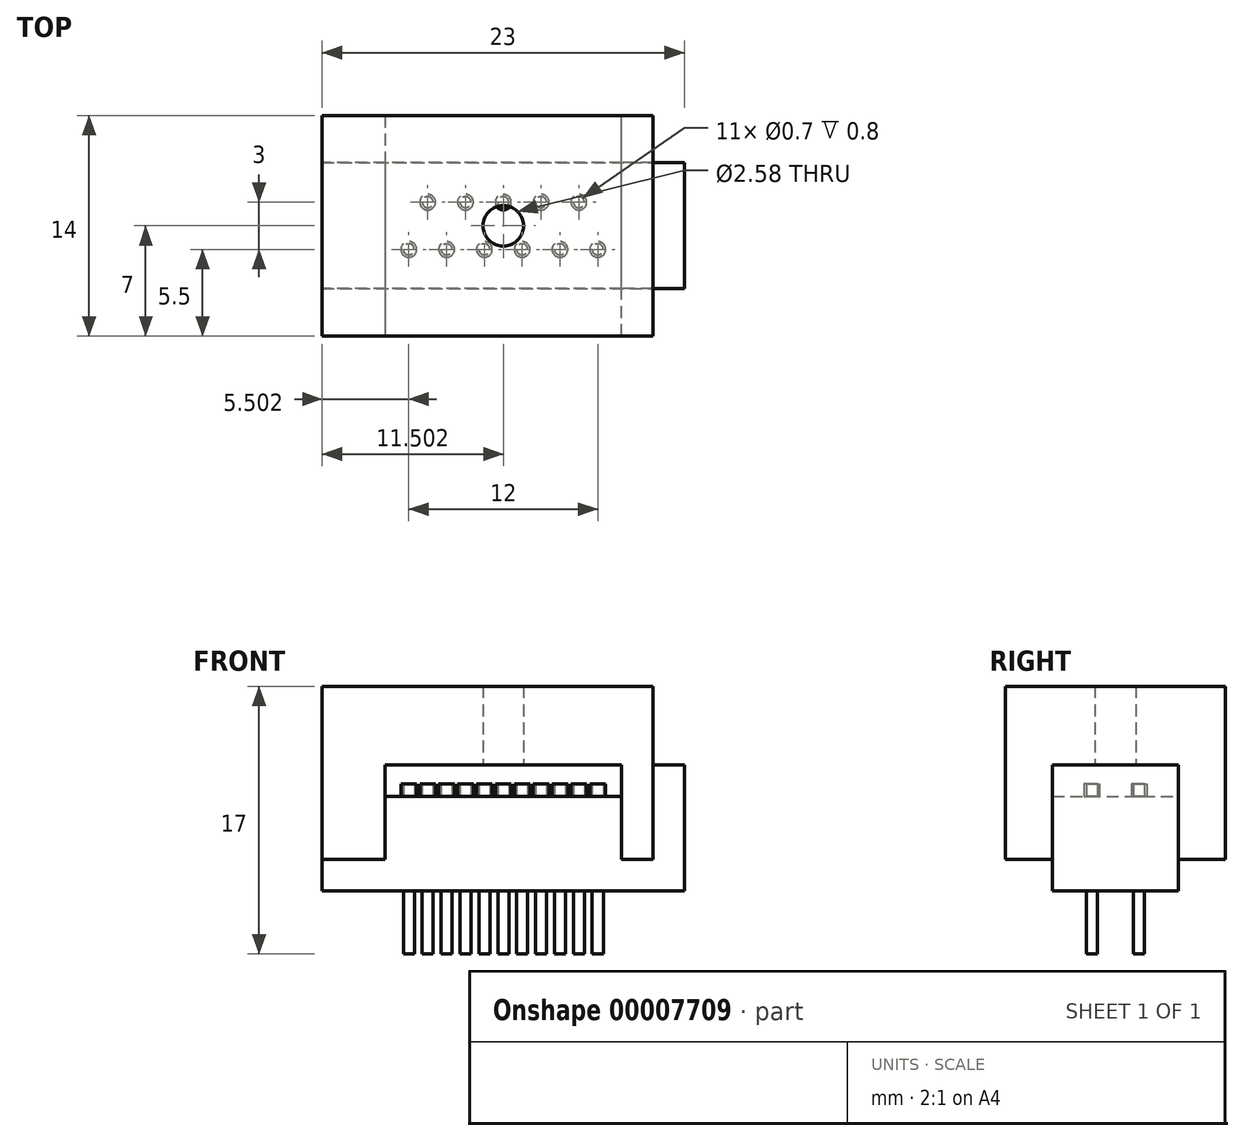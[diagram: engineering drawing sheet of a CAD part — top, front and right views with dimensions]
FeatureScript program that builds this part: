
annotation { "Feature Type Name" : "Feature", "Feature Type Description" : "" }
export const myFeature = defineFeature(function(context is Context, id is Id, definition is map)
    precondition{}
    {
        {
            var Q0;
            Q0=qCreatedBy(makeId("Front.planeOp"),FACE);
            var sketch = newSketch(context, id + "F0", { "sketchPlane" : qUnion([Q0])});
            skLineSegment(sketch, "E0", {"start": v(-36.77, -24.61) * mm, "end": v(-13.77, -24.61) * mm});
            skLineSegment(sketch, "E1", {"start": v(-13.77, -24.61) * mm, "end": v(-13.77, -16.61) * mm});
            skLineSegment(sketch, "E2", {"start": v(-13.77, -16.61) * mm, "end": v(-15.77, -16.61) * mm});
            skLineSegment(sketch, "E3", {"start": v(-15.77, -16.61) * mm, "end": v(-15.77, -18.61) * mm});
            skLineSegment(sketch, "E4", {"start": v(-15.77, -18.61) * mm, "end": v(-36.77, -18.61) * mm});
            skLineSegment(sketch, "E5", {"start": v(-36.77, -18.61) * mm, "end": v(-36.77, -24.61) * mm});
            skSolve(sketch);
        }
        {
            var Q0;
            Q0=makeQuery(id+"F0.imprint","IMPRINT",FACE,{"disambiguationData":[TD([[makeQuery(id+"F0.imprint","IMPRINT",EDGE,{"derivedFrom":sQuery(id+"F0.wireOp",EDGE,"E0")}),1.0]])]});
            extrude(context, id + "F1", {"entities" : qUnion([Q0]), "depth" : 8 * mm, "offsetDistance" : 25 * mm});
        }
        {
            var Q0;
            Q0=makeQuery(id+"F1.opExtrude","SWEPT_FACE",FACE,{"disambiguationData":[OSD([sQuery(id+"F0.wireOp",EDGE,"E4")])]});
            var sketch = newSketch(context, id + "F2", { "sketchPlane" : qUnion([Q0])});
            skLineSegment(sketch, "E6", {"start": v(-36.77, -4) * mm, "end": v(-15.77, -4) * mm, "construction": true});
            skLineSegment(sketch, "E7", {"start": v(-25.27, -8) * mm, "end": v(-25.27, 0) * mm, "construction": true});
            skLineSegment(sketch, "E8.0", {"start": v(-36.77, -2.5) * mm, "end": v(-15.77, -2.5) * mm, "construction": true});
            skLineSegment(sketch, "E9.0", {"start": v(-36.77, -5.5) * mm, "end": v(-15.77, -5.5) * mm, "construction": true});
            skCircle(sketch, "E10", {"center": v(-25.27, -2.5) * mm, "radius": 0.5 * mm});
            skLineSegment(sketch, "E11.1.0.0", {"start": v(-24.07, -8) * mm, "end": v(-24.07, 0) * mm, "construction": true});
            skLineSegment(sketch, "E11.2.0.0", {"start": v(-22.87, -8) * mm, "end": v(-22.87, 0) * mm, "construction": true});
            skLineSegment(sketch, "E11.3.0.0", {"start": v(-21.67, -8) * mm, "end": v(-21.67, 0) * mm, "construction": true});
            skLineSegment(sketch, "E11.4.0.0", {"start": v(-20.47, -8) * mm, "end": v(-20.47, 0) * mm, "construction": true});
            skLineSegment(sketch, "E11.5.0.0", {"start": v(-19.27, -8) * mm, "end": v(-19.27, 0) * mm, "construction": true});
            skLineSegment(sketch, "E11.6.0.0", {"start": v(-18.07, -8) * mm, "end": v(-18.07, 0) * mm, "construction": true});
            skLineSegment(sketch, "E11.7.0.0", {"start": v(-16.87, -8) * mm, "end": v(-16.87, 0) * mm, "construction": true});
            skLineSegment(sketch, "E11.direction1", {"start": v(-25.27, -8) * mm, "end": v(-24.07, -8) * mm, "construction": true});
            skLineSegment(sketch, "E12.1.0.0", {"start": v(-26.47, -8) * mm, "end": v(-26.47, 0) * mm, "construction": true});
            skLineSegment(sketch, "E12.2.0.0", {"start": v(-27.67, -8) * mm, "end": v(-27.67, 0) * mm, "construction": true});
            skLineSegment(sketch, "E12.3.0.0", {"start": v(-28.87, -8) * mm, "end": v(-28.87, 0) * mm, "construction": true});
            skLineSegment(sketch, "E12.4.0.0", {"start": v(-30.07, -8) * mm, "end": v(-30.07, 0) * mm, "construction": true});
            skLineSegment(sketch, "E12.5.0.0", {"start": v(-31.27, -8) * mm, "end": v(-31.27, 0) * mm, "construction": true});
            skLineSegment(sketch, "E12.6.0.0", {"start": v(-32.47, -8) * mm, "end": v(-32.47, 0) * mm, "construction": true});
            skLineSegment(sketch, "E12.7.0.0", {"start": v(-33.67, -8) * mm, "end": v(-33.67, 0) * mm, "construction": true});
            skLineSegment(sketch, "E12.direction1", {"start": v(-25.27, -8) * mm, "end": v(-26.47, -8) * mm, "construction": true});
            skCircle(sketch, "E13", {"center": v(-26.47, -5.5) * mm, "radius": 0.5 * mm});
            skCircle(sketch, "E14", {"center": v(-27.67, -2.5) * mm, "radius": 0.5 * mm});
            skCircle(sketch, "E15", {"center": v(-28.87, -5.5) * mm, "radius": 0.5 * mm});
            skCircle(sketch, "E16", {"center": v(-30.07, -2.5) * mm, "radius": 0.5 * mm});
            skCircle(sketch, "E17", {"center": v(-31.27, -5.5) * mm, "radius": 0.5 * mm});
            skCircle(sketch, "E18", {"center": v(-24.07, -5.5) * mm, "radius": 0.5 * mm});
            skCircle(sketch, "E19", {"center": v(-22.87, -2.5) * mm, "radius": 0.5 * mm});
            skCircle(sketch, "E20", {"center": v(-21.67, -5.5) * mm, "radius": 0.5 * mm});
            skCircle(sketch, "E21", {"center": v(-20.47, -2.5) * mm, "radius": 0.5 * mm});
            skCircle(sketch, "E22", {"center": v(-19.27, -5.5) * mm, "radius": 0.5 * mm});
            skCircle(sketch, "E23", {"center": v(-30.07, -2.5) * mm, "radius": 0.35 * mm});
            skCircle(sketch, "E24", {"center": v(-27.67, -2.5) * mm, "radius": 0.35 * mm});
            skCircle(sketch, "E25", {"center": v(-25.27, -2.5) * mm, "radius": 0.35 * mm});
            skCircle(sketch, "E26", {"center": v(-22.87, -2.5) * mm, "radius": 0.35 * mm});
            skCircle(sketch, "E27", {"center": v(-20.47, -2.5) * mm, "radius": 0.35 * mm});
            skCircle(sketch, "E28", {"center": v(-19.27, -5.5) * mm, "radius": 0.35 * mm});
            skCircle(sketch, "E29", {"center": v(-21.67, -5.5) * mm, "radius": 0.35 * mm});
            skCircle(sketch, "E30", {"center": v(-24.07, -5.5) * mm, "radius": 0.35 * mm});
            skCircle(sketch, "E31", {"center": v(-26.47, -5.5) * mm, "radius": 0.35 * mm});
            skCircle(sketch, "E32", {"center": v(-28.87, -5.5) * mm, "radius": 0.35 * mm});
            skCircle(sketch, "E33", {"center": v(-31.27, -5.5) * mm, "radius": 0.35 * mm});
            skSolve(sketch);
        }
        {
            var Q0;
            Q0=makeQuery(id+"F2.imprint","IMPRINT",FACE,{"disambiguationData":[TD([[makeQuery(id+"F2.imprint","IMPRINT",EDGE,{"derivedFrom":sQuery(id+"F2.wireOp",EDGE,"E23")}),1.0]])]});
            var Q1;
            Q1=makeQuery(id+"F2.imprint","IMPRINT",FACE,{"disambiguationData":[TD([[makeQuery(id+"F2.imprint","IMPRINT",EDGE,{"derivedFrom":sQuery(id+"F2.wireOp",EDGE,"E24")}),1.0]])]});
            var Q2;
            Q2=makeQuery(id+"F2.imprint","IMPRINT",FACE,{"disambiguationData":[TD([[makeQuery(id+"F2.imprint","IMPRINT",EDGE,{"derivedFrom":sQuery(id+"F2.wireOp",EDGE,"E25")}),1.0]])]});
            var Q3;
            Q3=makeQuery(id+"F2.imprint","IMPRINT",FACE,{"disambiguationData":[TD([[makeQuery(id+"F2.imprint","IMPRINT",EDGE,{"derivedFrom":sQuery(id+"F2.wireOp",EDGE,"E26")}),1.0]])]});
            var Q4;
            Q4=makeQuery(id+"F2.imprint","IMPRINT",FACE,{"disambiguationData":[TD([[makeQuery(id+"F2.imprint","IMPRINT",EDGE,{"derivedFrom":sQuery(id+"F2.wireOp",EDGE,"E27")}),1.0]])]});
            var Q5;
            Q5=makeQuery(id+"F2.imprint","IMPRINT",FACE,{"disambiguationData":[TD([[makeQuery(id+"F2.imprint","IMPRINT",EDGE,{"derivedFrom":sQuery(id+"F2.wireOp",EDGE,"E28")}),1.0]])]});
            var Q6;
            Q6=makeQuery(id+"F2.imprint","IMPRINT",FACE,{"disambiguationData":[TD([[makeQuery(id+"F2.imprint","IMPRINT",EDGE,{"derivedFrom":sQuery(id+"F2.wireOp",EDGE,"E29")}),1.0]])]});
            var Q7;
            Q7=makeQuery(id+"F2.imprint","IMPRINT",FACE,{"disambiguationData":[TD([[makeQuery(id+"F2.imprint","IMPRINT",EDGE,{"derivedFrom":sQuery(id+"F2.wireOp",EDGE,"E30")}),1.0]])]});
            var Q8;
            Q8=makeQuery(id+"F2.imprint","IMPRINT",FACE,{"disambiguationData":[TD([[makeQuery(id+"F2.imprint","IMPRINT",EDGE,{"derivedFrom":sQuery(id+"F2.wireOp",EDGE,"E31")}),1.0]])]});
            var Q9;
            Q9=makeQuery(id+"F2.imprint","IMPRINT",FACE,{"disambiguationData":[TD([[makeQuery(id+"F2.imprint","IMPRINT",EDGE,{"derivedFrom":sQuery(id+"F2.wireOp",EDGE,"E32")}),1.0]])]});
            var Q10;
            Q10=makeQuery(id+"F2.imprint","IMPRINT",FACE,{"disambiguationData":[TD([[makeQuery(id+"F2.imprint","IMPRINT",EDGE,{"derivedFrom":sQuery(id+"F2.wireOp",EDGE,"E33")}),1.0]])]});
            extrude(context, id + "F3", {"entities" : qUnion([Q0, Q1, Q2, Q3, Q4, Q5, Q6, Q7, Q8, Q9, Q10]), "operationType" : NewBodyOperationType.ADD, "oppositeDirection" : true, "depth" : 10 * mm, "offsetDistance" : 25 * mm});
        }
        {
            var Q0;
            Q0=makeQuery(id+"F2.imprint","IMPRINT",FACE,{"disambiguationData":[TD([[makeQuery(id+"F2.imprint","IMPRINT",EDGE,{"derivedFrom":sQuery(id+"F2.wireOp",EDGE,"E16")}),1.0]])]});
            var Q1;
            Q1=makeQuery(id+"F2.imprint","IMPRINT",FACE,{"disambiguationData":[TD([[makeQuery(id+"F2.imprint","IMPRINT",EDGE,{"derivedFrom":sQuery(id+"F2.wireOp",EDGE,"E14")}),1.0]])]});
            var Q2;
            Q2=makeQuery(id+"F2.imprint","IMPRINT",FACE,{"disambiguationData":[TD([[makeQuery(id+"F2.imprint","IMPRINT",EDGE,{"derivedFrom":sQuery(id+"F2.wireOp",EDGE,"E17")}),1.0]])]});
            var Q3;
            Q3=makeQuery(id+"F2.imprint","IMPRINT",FACE,{"disambiguationData":[TD([[makeQuery(id+"F2.imprint","IMPRINT",EDGE,{"derivedFrom":sQuery(id+"F2.wireOp",EDGE,"E15")}),1.0]])]});
            var Q4;
            Q4=makeQuery(id+"F2.imprint","IMPRINT",FACE,{"disambiguationData":[TD([[makeQuery(id+"F2.imprint","IMPRINT",EDGE,{"derivedFrom":sQuery(id+"F2.wireOp",EDGE,"E13")}),1.0]])]});
            var Q5;
            Q5=makeQuery(id+"F2.imprint","IMPRINT",FACE,{"disambiguationData":[TD([[makeQuery(id+"F2.imprint","IMPRINT",EDGE,{"derivedFrom":sQuery(id+"F2.wireOp",EDGE,"E18")}),1.0]])]});
            var Q6;
            Q6=makeQuery(id+"F2.imprint","IMPRINT",FACE,{"disambiguationData":[TD([[makeQuery(id+"F2.imprint","IMPRINT",EDGE,{"derivedFrom":sQuery(id+"F2.wireOp",EDGE,"E20")}),1.0]])]});
            var Q7;
            Q7=makeQuery(id+"F2.imprint","IMPRINT",FACE,{"disambiguationData":[TD([[makeQuery(id+"F2.imprint","IMPRINT",EDGE,{"derivedFrom":sQuery(id+"F2.wireOp",EDGE,"E22")}),1.0]])]});
            var Q8;
            Q8=makeQuery(id+"F2.imprint","IMPRINT",FACE,{"disambiguationData":[TD([[makeQuery(id+"F2.imprint","IMPRINT",EDGE,{"derivedFrom":sQuery(id+"F2.wireOp",EDGE,"E21")}),1.0]])]});
            var Q9;
            Q9=makeQuery(id+"F2.imprint","IMPRINT",FACE,{"disambiguationData":[TD([[makeQuery(id+"F2.imprint","IMPRINT",EDGE,{"derivedFrom":sQuery(id+"F2.wireOp",EDGE,"E19")}),1.0]])]});
            var Q10;
            Q10=makeQuery(id+"F2.imprint","IMPRINT",FACE,{"disambiguationData":[TD([[makeQuery(id+"F2.imprint","IMPRINT",EDGE,{"derivedFrom":sQuery(id+"F2.wireOp",EDGE,"E10")}),1.0]])]});
            extrude(context, id + "F4", {"entities" : qUnion([Q0, Q1, Q2, Q3, Q4, Q5, Q6, Q7, Q8, Q9, Q10]), "operationType" : NewBodyOperationType.ADD, "depth" : .8 * mm, "offsetDistance" : 25 * mm});
        }
        {
            var Q0;
            Q0=makeQuery(id+"F1.opExtrude","SWEPT_FACE",FACE,{"disambiguationData":[OSD([sQuery(id+"F0.wireOp",EDGE,"E2")])]});
            var sketch = newSketch(context, id + "F5", { "sketchPlane" : qUnion([Q0])});
            skLineSegment(sketch, "E34.0", {"start": v(-15.77, 0) * mm, "end": v(-36.77, 0) * mm});
            skLineSegment(sketch, "E34.1", {"start": v(-36.77, -8) * mm, "end": v(-36.77, 0) * mm, "construction": true});
            skLineSegment(sketch, "E34.2", {"start": v(-15.77, -8) * mm, "end": v(-36.77, -8) * mm});
            skCircle(sketch, "E35.0", {"center": v(-31.27, -5.5) * mm, "radius": 0.5 * mm, "construction": true});
            skCircle(sketch, "E35.1", {"center": v(-19.27, -5.5) * mm, "radius": 0.5 * mm, "construction": true});
            skLineSegment(sketch, "E36", {"start": v(-31.77, 0) * mm, "end": v(-31.77, -8) * mm, "construction": true});
            skLineSegment(sketch, "E37", {"start": v(-18.77, -8) * mm, "end": v(-18.77, 0) * mm, "construction": true});
            skLineSegment(sketch, "E38.0", {"start": v(-32.77, 3) * mm, "end": v(-32.77, -11) * mm});
            skLineSegment(sketch, "E39.0", {"start": v(-36.77, 3) * mm, "end": v(-36.77, -11) * mm});
            skLineSegment(sketch, "E40.0", {"start": v(-17.77, -11) * mm, "end": v(-17.77, 3) * mm});
            skLineSegment(sketch, "E41.0", {"start": v(-15.77, -11) * mm, "end": v(-15.77, 3) * mm});
            skLineSegment(sketch, "E42.0", {"start": v(-15.77, 3) * mm, "end": v(-36.77, 3) * mm});
            skLineSegment(sketch, "E43.0", {"start": v(-15.77, -11) * mm, "end": v(-36.77, -11) * mm});
            skLineSegment(sketch, "E44", {"start": v(-36.77, 0) * mm, "end": v(-36.77, 0) * mm});
            skLineSegment(sketch, "E45", {"start": v(-36.77, -8) * mm, "end": v(-36.77, -8) * mm});
            skLineSegment(sketch, "E46", {"start": v(-26.27, -11) * mm, "end": v(-26.27, 3) * mm, "construction": true});
            skCircle(sketch, "E47", {"center": v(-25.27, -4) * mm, "radius": 1.29 * mm});
            skLineSegment(sketch, "E48", {"start": v(-36.77, -4) * mm, "end": v(-13.77, -4) * mm, "construction": true});
            skSolve(sketch);
        }
        {
            var Q0;
            {var subQ0=sQuery(id+"F5.wireOp",EDGE,"E40.0");var subQ1=sQuery(id+"F5.wireOp",EDGE,"E34.0");var subQ2=makeQuery(id+"F5.imprint","INTERSECT",VERTEX,{"derivedFrom":[subQ1,subQ0]});Q0=makeQuery(id+"F5.imprint","IMPRINT",FACE,{"disambiguationData":[TD([[makeQuery(id+"F5.imprint","IMPRINT",EDGE,{"disambiguationData":[TD([[subQ2,-1.0]])],"derivedFrom":subQ1}),1.0]])]});}
            var Q1;
            {var subQ0=sQuery(id+"F5.wireOp",EDGE,"E40.0");var subQ1=sQuery(id+"F5.wireOp",EDGE,"E34.0");var subQ2=makeQuery(id+"F5.imprint","INTERSECT",VERTEX,{"derivedFrom":[subQ1,subQ0]});Q1=makeQuery(id+"F5.imprint","IMPRINT",FACE,{"disambiguationData":[TD([[makeQuery(id+"F5.imprint","IMPRINT",EDGE,{"disambiguationData":[TD([[subQ2,-1.0]])],"derivedFrom":subQ1}),-1.0]])]});}
            var Q2;
            {var subQ0=sQuery(id+"F5.wireOp",EDGE,"E40.0");var subQ1=sQuery(id+"F5.wireOp",EDGE,"E34.2");var subQ2=makeQuery(id+"F5.imprint","INTERSECT",VERTEX,{"derivedFrom":[subQ1,subQ0]});Q2=makeQuery(id+"F5.imprint","IMPRINT",FACE,{"disambiguationData":[TD([[makeQuery(id+"F5.imprint","IMPRINT",EDGE,{"disambiguationData":[TD([[subQ2,-1.0]])],"derivedFrom":subQ1}),1.0]])]});}
            extrude(context, id + "F6", {"entities" : qUnion([Q0, Q1, Q2]), "depth" : 5 * mm, "offsetDistance" : 25 * mm});
        }
        {
            var Q0;
            {var subQ0=sQuery(id+"F5.wireOp",EDGE,"E39.0");var subQ1=sQuery(id+"F5.wireOp",EDGE,"E34.0");var subQ2=makeQuery(id+"F5.imprint","INTERSECT",VERTEX,{"derivedFrom":[subQ1,subQ0]});Q0=makeQuery(id+"F5.imprint","IMPRINT",FACE,{"disambiguationData":[TD([[makeQuery(id+"F5.imprint","IMPRINT",EDGE,{"disambiguationData":[TD([[subQ2,1.0]])],"derivedFrom":subQ1}),1.0]])]});}
            var Q1;
            {var subQ1=sQuery(id+"F5.wireOp",EDGE,"E34.0");var subQ4=sQuery(id+"F5.wireOp",EDGE,"E40.0");var subQ5=makeQuery(id+"F5.imprint","INTERSECT",VERTEX,{"derivedFrom":[subQ1,subQ4]});Q1=makeQuery(id+"F5.imprint","IMPRINT",FACE,{"disambiguationData":[TD([[makeQuery(id+"F5.imprint","IMPRINT",EDGE,{"disambiguationData":[TD([[subQ5,1.0]])],"derivedFrom":subQ4}),-1.0]])]});}
            extrude(context, id + "F7", {"entities" : qUnion([Q0, Q1]), "operationType" : NewBodyOperationType.ADD, "depth" : 5 * mm, "offsetDistance" : 25 * mm, "hasSecondDirection" : true, "secondDirectionOppositeDirection" : true, "secondDirectionDepth" : 2 * mm});
        }
        {
            var Q0;
            {var subQ0=sQuery(id+"F5.wireOp",EDGE,"E39.0");var subQ1=sQuery(id+"F5.wireOp",EDGE,"E34.2");var subQ2=makeQuery(id+"F5.imprint","INTERSECT",VERTEX,{"derivedFrom":[subQ1,subQ0]});Q0=makeQuery(id+"F5.imprint","IMPRINT",FACE,{"disambiguationData":[TD([[makeQuery(id+"F5.imprint","IMPRINT",EDGE,{"disambiguationData":[TD([[subQ2,1.0]])],"derivedFrom":subQ1}),1.0]])]});}
            var Q1;
            {var subQ3=sQuery(id+"F5.wireOp",EDGE,"E40.0");var subQ5=sQuery(id+"F5.wireOp",EDGE,"E43.0");var subQ6=makeQuery(id+"F5.imprint","INTERSECT",VERTEX,{"derivedFrom":[subQ3,subQ5]});Q1=makeQuery(id+"F5.imprint","IMPRINT",FACE,{"disambiguationData":[TD([[makeQuery(id+"F5.imprint","IMPRINT",EDGE,{"disambiguationData":[TD([[subQ6,-1.0]])],"derivedFrom":subQ3}),-1.0]])]});}
            var Q2;
            {var subQ0=sQuery(id+"F5.wireOp",EDGE,"E39.0");var subQ1=sQuery(id+"F5.wireOp",EDGE,"E34.0");var subQ2=makeQuery(id+"F5.imprint","INTERSECT",VERTEX,{"derivedFrom":[subQ1,subQ0]});Q2=makeQuery(id+"F5.imprint","IMPRINT",FACE,{"disambiguationData":[TD([[makeQuery(id+"F5.imprint","IMPRINT",EDGE,{"disambiguationData":[TD([[subQ2,1.0]])],"derivedFrom":subQ1}),-1.0]])]});}
            var Q3;
            {var subQ3=sQuery(id+"F5.wireOp",EDGE,"E40.0");var subQ5=sQuery(id+"F5.wireOp",EDGE,"E42.0");var subQ6=makeQuery(id+"F5.imprint","INTERSECT",VERTEX,{"derivedFrom":[subQ3,subQ5]});Q3=makeQuery(id+"F5.imprint","IMPRINT",FACE,{"disambiguationData":[TD([[makeQuery(id+"F5.imprint","IMPRINT",EDGE,{"disambiguationData":[TD([[subQ6,1.0]])],"derivedFrom":subQ3}),-1.0]])]});}
            extrude(context, id + "F8", {"entities" : qUnion([Q0, Q1, Q2, Q3]), "operationType" : NewBodyOperationType.ADD, "depth" : 5 * mm, "offsetDistance" : 25 * mm, "hasSecondDirection" : true, "secondDirectionOppositeDirection" : true, "secondDirectionDepth" : 6 * mm});
        }
    });
